# Revit family: PRD_FrankeWS_ShwrMxrs_SelfClosingShowerMixer_F5ST2001-2003,2009_V1
name_source: partatom
category: Plumbing Fixtures
revit_build: Autodesk Revit 2018 (Build: 20190510_1515(x64)
units: mm (PartAtom-declared; Revit-internal decimal feet)

## family parameters
Cut with Voids When Loaded = No
Host = Face
OmniClass Number = 23.45.05.14.99
OmniClass Title = Other Sanitary Washing Plumbing Fixtures
Part Type = Normal
Room Calculation Point = No
Round Connector Dimension = Use Diameter
Shared = No

## types (4) — shared parameters
AdditionalConnections = no
AdjustableFlowTime = yes
AssetType = Fixed
Category = Pr_40_20_87_81, Shower thermostatic water supply sets
Circulation = no
CloseOffRating = 0.0 Pa
Color = Chrome
ConnectionWithPayWaterDispenser = not possible
Default Elevation = 850 mm  [stored 2.78871 ft]
DiameterNominal = 15.000 mm
DurationUnit = year
Features = For shower facilities, connects to hot and cold water. All-metal construction, high-polished chromium-plated brass.
Finish = high-polished chromium-plated brass
FlowCoefficient = 0
FlowColdWater = 0.2 L/s
FlowHotWater = 0.2 L/s
FunctionalPrinciple = hydraulic self-closing
IfcExportAs = IfcValveType
IfcExportType = MIXING
InletSize = G-1-2-B
Manufacturer = KWC Group AG
ManufacturerName = KWC Group AG
ManufacturerURL = www.kwc.com
Material = Brass
MaterialsBody = Brass
MaximumFlowTime = 35.00 seconds
MinimumFlowPressure = 1.00 bar
MinimumFlowTime = 5.00 seconds
MixerControl = Other
NBSDescription = Shower thermostatic water supply sets
NBSReference = 45-35-70/335
OutletConnectionSize = 15 mm  [stored 0.0492126 ft]
PositionOfWaterConnection = from backside
ProductInformation = https://pim.kwc.com
ProtectiveShutdown = no
SensorMaterial = PRD_AR_SyntheticDarkGrey
SoundInsulation = no
TapMaterial = PRD_AR_ChromatedBrass_HighPolished
TestPressure = 0.0 Pa
ThermalDisinfection = manual thermal disinfection
TypeOfMixing = with thermostat
TypeOfMounting = Wall mounting
TypeOfOperation = manual operation
TypeOfShower = wall fitting
URL = www.kwc.com
Uniclass2015Code = Pr_40_20_87_81
Uniclass2015Title = Shower thermostatic water supply sets
Uniclass2015Version = Products v1.10
ValveMechanism = Other
ValveOperation = Other
ValvePattern = ANGLED_2_PORT
Version = 1
WarrantyDurationUnit = year
zero-valued in all types: NominalHeight, NominalLength

## per-type parameters (varying)
| type | BIMObjectName | Cap | DefaultAutomaticHygieneFlushing | Description | GrossWeight | HygieneFlushing | HygieneUnit | Model | ModelNumber | ModelReference | Name | NetWeight | NominalWidth | OutletBottom | OutletTop | PowerConsumption | PowerSupplyConnection | ProtectiveSystemIP | ShowerPipeDraining | ShowerPipeEmptying | TypeOfSensor | VolumeFlowRate |
| F5ST2001 - 0.30 L/s, top outlet | PRD_AR_ShowerMixers_SelfClosingShowerMixer_F5ST2001 | Yes |  | F5S-Therm self-closing thermostatic wall-mounted mixer DN 15 for wall mounting, for shower facilities. Hydraulically controlled, connects to hot and cold water. With a mechanism for an optional water hygiene unit for automatic water hygiene flushing and storage of statistical data. FRAMIC self-closing cartridge, hydraulically controlled, low-maintenance and stagnation-free, with ceramic disc technology, self-closing, flow pressure-independent due to medium-separated design. Stepless adjustment of flow duration. Thermostat with metal handle with adjustable and turn-proof temperature stop, with the option for a manual thermal disinfection. Scald-protected Safe-Touch housing with outlet on top, G 3/4 B, for installation of bent outlet or wall-mounted shower pipe. All-metal construction, high-polished chromium-plated brass. With adjustable and turn-proof connections with backflow preventer and strainers, completely covered with depth-adjustable screw rosettes. | 4.00 kg | prepared | No | F5ST2001 | 2030032978 | F5ST2001 | F5 self-closing shower mixer F5ST2001 | 3.80 kg | 263 mm  [stored 0.862861 ft] | No | Yes |  |  |  | no | No |  | 0.30 L/s at 3 bar |
| F5ST2002 - 0.30 L/s, top outlet with shower pipe draining | PRD_AR_ShowerMixers_SelfClosingShowerMixer_F5ST2002 | Yes |  | F5S-Therm self-closing thermostatic wall-mounted mixer DN 15 for wall mounting, for shower facilities. Hydraulically controlled, connects to hot and cold water. With a mechanism for an optional water hygiene unit for automatic water hygiene flushing and storage of statistical data. FRAMIC self-closing cartridge, hydraulically controlled, low-maintenance and stagnation-free, with ceramic disc technology, self-closing, flow pressure-independent due to medium-separated design. Stepless adjustment of flow duration. Thermostat with metal handle with adjustable and turn-proof temperature stop, with the option for a manual thermal disinfection. Scald-protected Safe-Touch housing with outlet on top, G 3/4 B, for installation of bent outlet or wall-mounted shower pipe. All-metal construction, high-polished chromium-plated brass. With adjustable and turn-proof connections with backflow preventer and strainers, completely covered with depth-adjustable screw rosettes. Version with automatic shower pipe draining. | 4.20 kg | prepared | No | F5ST2002 | 2030036208 | F5ST2002 | F5 self-closing shower mixer F5ST2002 | 4.00 kg | 263 mm  [stored 0.862861 ft] | No | Yes |  |  |  | yes | Yes |  | 0.30 L/s at 3 bar |
| F5ST2003 - 0.30 L/s, bottom outlet | PRD_AR_ShowerMixers_SelfClosingShowerMixer_F5ST2003 | Yes |  | F5S-Therm self-closing thermostatic wall-mounted mixer DN 15 for wall mounting, for shower facilities. Hydraulically controlled, connects to hot and cold water. With a mechanism for an optional water hygiene unit for automatic water hygiene flushing and storage of statistical data. FRAMIC self-closing cartridge, hydraulically controlled, low-maintenance and stagnation-free, with ceramic disc technology, self-closing, flow pressure-independent due to medium-separated design. Stepless adjustment of flow duration. Thermostat with metal handle with adjustable and turn-proof temperature stop, with the option for a manual thermal disinfection. Scald-protected, Safe-Touch housing with hand shower connection, G 1/2 B. All-metal construction, high-polished chromium-plated brass. With adjustable and turn-proof connections with backflow preventer and strainers, completely covered with depth-adjustable screw rosettes. | 3.90 kg | prepared | No | F5ST2003 | 2030036209 | F5ST2003 | F5 self-closing shower mixer F5ST2003 | 3.70 kg | 263 mm  [stored 0.862861 ft] | Yes | No |  |  |  | no | No |  | 0.30 L/s at 3 bar |
| F5ST2009 - 0.20 L/s, top outlet with hygiene unit | PRD_AR_ShowerMixers_SelfClosingShowerMixer_F5ST2009 | No | fixed interval 24 hours | F5S-Therm self-closing thermostatic wall-mounted mixer DN 15 for wall mounting, for shower facilities. Hydraulically controlled, connects to hot and cold water. With a pre-assembled hygiene unit including sensor with control electronics and 6 V lithium battery (CR-P2) for performing an automatic water hygiene flushing and storage of statistical data. FRAMIC self-closing cartridge, hydraulically controlled, low-maintenance and stagnation-free, with ceramic disc technology, self-closing, flow pressure-independent due to medium-separated design. Stepless adjustment of flow duration. Thermostat with metal handle with adjustable and turn-proof temperature stop, with the option for a manual thermal disinfection. Scald-protected Safe-Touch housing with outlet on top, G 3/4 B, for installation of bent outlet or wall-mounted shower pipe. All-metal construction, high-polished chromium-plated brass. With adjustable and turn-proof connections with backflow preventer and strainers, completely covered with depth-adjustable screw rosettes. Activated water hygiene flushing, fixed interval of 24 hours. With option for parameterization and communication via optional, bidirectional remote control. | 4.60 kg | yes | Yes | F5ST2009 | 2030040291 | F5ST2009 | F5 self-closing shower mixer F5ST2009 | 4.40 kg | 317 mm  [stored 1.04003 ft] | No | Yes | 1.5 | Battery 6 V | IP59K | no | No | opto-electronic sensor | 0.20 L/s at 3 bar |

note: [stored X ft] marks values corroborated as IEEE doubles in the binary element streams (Revit-internal decimal feet)

## geometry (parser evidence)
native form markers: Sweep x2
no freeform markers — native parametric forms only
